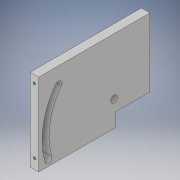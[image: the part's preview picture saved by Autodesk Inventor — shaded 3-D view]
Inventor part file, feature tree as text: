
AUTODESK INVENTOR PART (.ipt)
format: ipt  version: 2019 (Build 230136000, 136)  size: 139,776 bytes
history: native  units: in
note: dims shown in document units (in); Inventor stores cm internally (conversion verified against a paired STEP export)
features: sketch x3, extrude x2, hole x2, projected_geometry x2, other x1
ambient origin geometry x8: Origin, YZ Plane, XZ Plane, XY Plane, X Axis, Y Axis, Z Axis, Center Point
bodies: Solid1 (feature_tree)
feature tree (10):
  other  "third odomitry wheel"
  extrude  "Extrusion1"  Depth=2.0in
  extrude  "Extrusion2"  Depth=0.35in
  sketch  "Sketch6"  dims[d2=0.25in d3=0.0in d4=0.35in]
  sketch  "Sketch7"  dims[d7=0.2in d8=0.25in d9=0.0in d27=1.0in d28=0.4in d29=0.076in d30=0.198in d31=0.375in d32=0.25in d33=0.5635in d34=0.302in d35=0.8108in d36=0.076in d37=0.198in d38=0.375in d39=0.25in d40=0.5635in d41=0.302in d42=0.8108in d43=0.05in d44=0.3588in d46=0.1in d47=2.0in]
  hole  "Hole2"  [1 undecoded]
  hole  "Hole3"  [1 undecoded]
  sketch  "Sketch2"  dims[d0=3.25in d1=2.0in]
  projected_geometry  "Projected Loop2"
  projected_geometry  "Projected Loop3"
note: 2 required parameter values undecoded (feature->parameter linkage not recoverable at this tier; creation-order binding heuristic only, values carry confidence <= 0.55)
